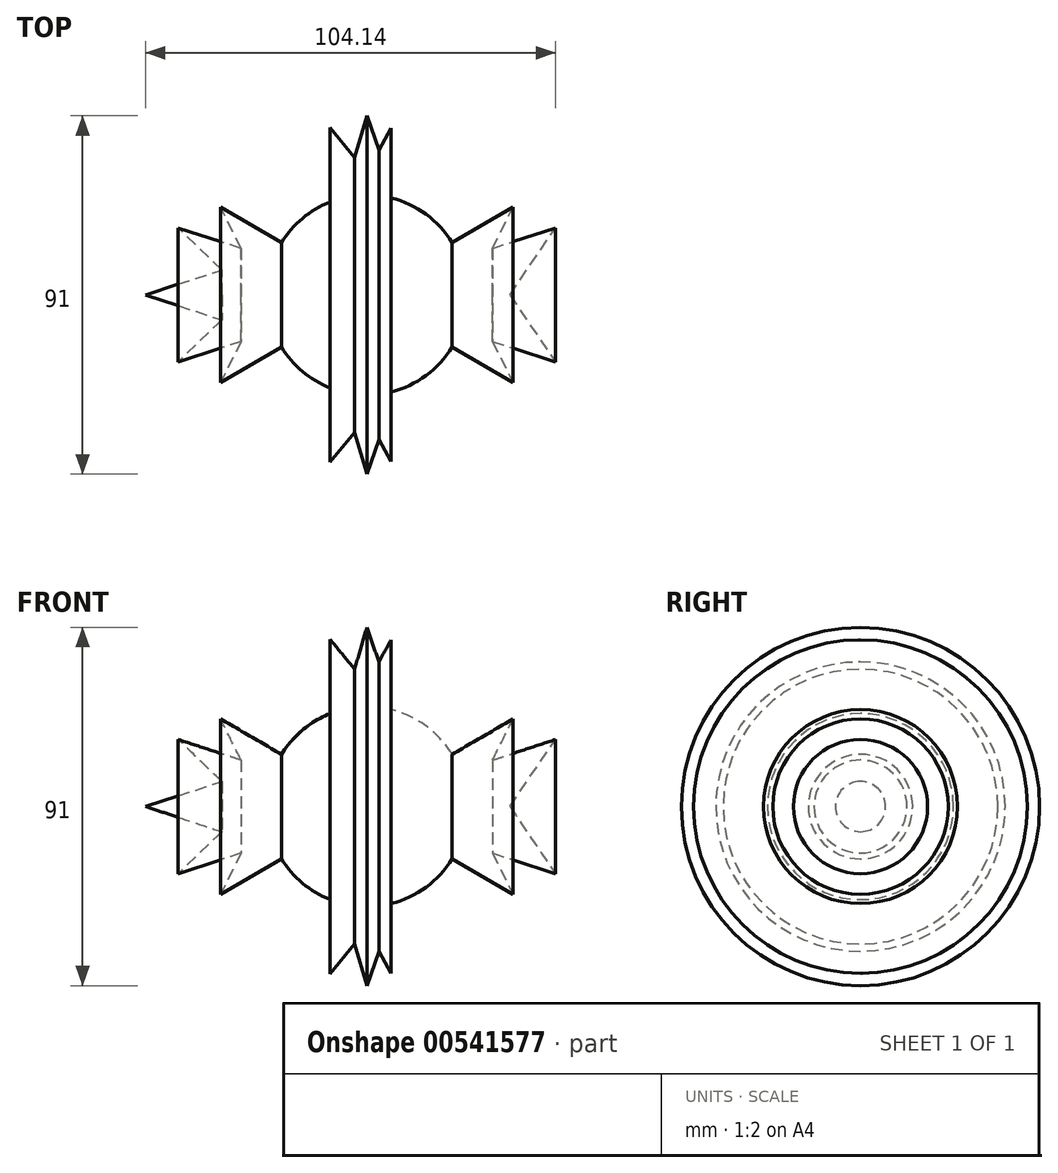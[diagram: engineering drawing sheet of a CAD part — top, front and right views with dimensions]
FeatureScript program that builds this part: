
annotation { "Feature Type Name" : "Feature", "Feature Type Description" : "" }
export const myFeature = defineFeature(function(context is Context, id is Id, definition is map)
    precondition{}
    {
        {
            var Q0;
            Q0=qCreatedBy(makeId("Top.planeOp"),FACE);
            var sketch = newSketch(context, id + "F0", { "sketchPlane" : qUnion([Q0])});
            skArc(sketch, "E0", {"start": v(21.66, 13.27) * mm, "mid": v(15.03, 20.48) * mm, "end": v(6.16, 24.64) * mm});
            skLineSegment(sketch, "E1", {"start": v(21.66, 13.27) * mm, "end": v(37.2, 22.3) * mm});
            skLineSegment(sketch, "E2", {"start": v(37.2, 22.3) * mm, "end": v(31.91, 11.8) * mm});
            skLineSegment(sketch, "E3", {"start": v(31.91, 11.8) * mm, "end": v(47.92, 17.04) * mm});
            skPoint(sketch, "E3.endSnap0", {"position": v(34.55, 17.04) * mm});
            skLineSegment(sketch, "E4", {"start": v(47.92, 17.04) * mm, "end": v(36.33, 0) * mm});
            skLineSegment(sketch, "E5", {"start": v(0, 25.4) * mm, "end": v(0, 25.4) * mm});
            skLineSegment(sketch, "E6.MirrorCS", {"start": v(-21.66, 13.27) * mm, "end": v(-37.2, 22.3) * mm});
            skLineSegment(sketch, "E7.MirrorCS", {"start": v(-37.2, 22.3) * mm, "end": v(-31.91, 11.8) * mm});
            skLineSegment(sketch, "E8.MirrorCS", {"start": v(-31.91, 11.8) * mm, "end": v(-47.92, 17.04) * mm});
            skLineSegment(sketch, "E9.MirrorCS", {"start": v(-47.92, 17.04) * mm, "end": v(-36.84, 6.38) * mm});
            skLineSegment(sketch, "E10.MirrorCS", {"start": v(-36.84, 6.38) * mm, "end": v(-56.22, 0) * mm});
            skLineSegment(sketch, "E11.MirrorCS", {"start": v(-56.22, 0) * mm, "end": v(36.33, 0) * mm});
            skLineSegment(sketch, "E12", {"start": v(-9.32, 23.63) * mm, "end": v(-9.32, 42.48) * mm});
            skLineSegment(sketch, "E13", {"start": v(-9.32, 42.48) * mm, "end": v(-9.32, 42.48) * mm});
            skLineSegment(sketch, "E14", {"start": v(-9.32, 42.48) * mm, "end": v(-3.1, 34.9) * mm});
            skLineSegment(sketch, "E15", {"start": v(3.08, 36.76) * mm, "end": v(6.16, 42.38) * mm});
            skLineSegment(sketch, "E16", {"start": v(6.16, 42.38) * mm, "end": v(6.16, 24.64) * mm});
            skLineSegment(sketch, "E17", {"start": v(-3.1, 34.9) * mm, "end": v(-3.1, 34.9) * mm});
            skLineSegment(sketch, "E18", {"start": v(-3.1, 34.9) * mm, "end": v(0, 45.5) * mm});
            skLineSegment(sketch, "E19", {"start": v(0, 45.5) * mm, "end": v(3.08, 36.76) * mm});
            skArc(sketch, "E20.trimOffspring", {"start": v(-9.32, 23.63) * mm, "mid": v(-16.33, 19.45) * mm, "end": v(-21.66, 13.27) * mm});
            skPoint(sketch, "E21.orphan", {"position": v(0, 31.14) * mm});
            skPoint(sketch, "E22.end.orphan", {"position": v(25.4, 0) * mm});
            skPoint(sketch, "E23.end.orphan", {"position": v(56.73, 0) * mm});
            skSolve(sketch);
        }
        {
            var Q0;
            {var subQ2=sQuery(id+"F0.wireOp",EDGE,"E6.MirrorCS");Q0=makeQuery(id+"F0.imprint","IMPRINT",FACE,{"disambiguationData":[TD([[makeQuery(id+"F0.imprint","IMPRINT",EDGE,{"derivedFrom":subQ2}),1.0]])]});}
            var Q1;
            {var subQ3=sQuery(id+"F0.wireOp",EDGE,"bbc177cd-0adc-4325-be5c-051ec6b3b3ad");Q1=makeQuery(id+"F0.imprint","IMPRINT",FACE,{"disambiguationData":[TD([[makeQuery(id+"F0.imprint","IMPRINT",EDGE,{"derivedFrom":subQ3}),1.0]])]});}
            var Q2;
            {var subQ3=sQuery(id+"F0.wireOp",EDGE,"bbc177cd-0adc-4325-be5c-051ec6b3b3ad");Q2=makeQuery(id+"F0.imprint","IMPRINT",FACE,{"disambiguationData":[TD([[makeQuery(id+"F0.imprint","IMPRINT",EDGE,{"derivedFrom":subQ3}),-1.0]])]});}
            var Q3;
            {var subQ0=sQuery(id+"F0.wireOp",EDGE,"E1");Q3=makeQuery(id+"F0.imprint","IMPRINT",FACE,{"disambiguationData":[TD([[makeQuery(id+"F0.imprint","IMPRINT",EDGE,{"derivedFrom":subQ0}),-1.0]])]});}
            var Q4;
            {var subQ0=sQuery(id+"F0.wireOp",EDGE,"E12");Q4=makeQuery(id+"F0.imprint","IMPRINT",FACE,{"disambiguationData":[TD([[makeQuery(id+"F0.imprint","IMPRINT",EDGE,{"derivedFrom":subQ0}),-1.0]])]});}
            var Q5;
            {var subQ3=sQuery(id+"F0.wireOp",EDGE,"E18");Q5=makeQuery(id+"F0.imprint","IMPRINT",FACE,{"disambiguationData":[TD([[makeQuery(id+"F0.imprint","IMPRINT",EDGE,{"derivedFrom":subQ3}),-1.0]])]});}
            var Q6;
            Q6=sQuery(id+"F0.wireOp",EDGE,"E11.MirrorCS");
            revolve(context, id + "F1", {"entities" : qUnion([Q0, Q1, Q2, Q3, Q4, Q5]), "axis" : qUnion([Q6]), "revolveType" : RevolveType.FULL});
        }
    });
